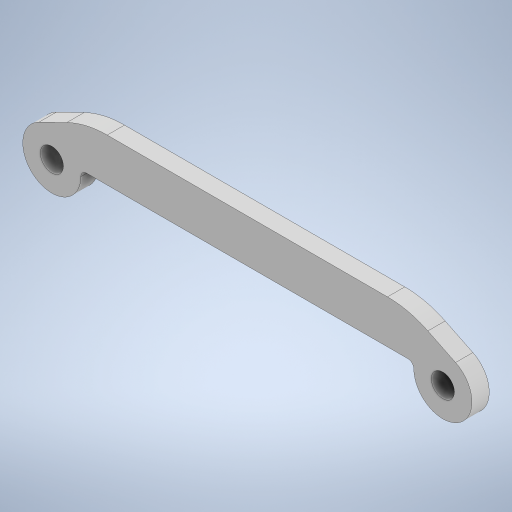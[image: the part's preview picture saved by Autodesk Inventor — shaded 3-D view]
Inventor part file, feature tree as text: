
AUTODESK INVENTOR PART (.ipt)
format: ipt  version: 2024 (Build 280153000, 153)  size: 267,776 bytes
history: native  units: in
note: dims shown in document units (in); Inventor stores cm internally (conversion verified against a paired STEP export)
features: fillet x2, extrude x1, sketch x1
ambient origin geometry x8: Origin, YZ Plane, XZ Plane, XY Plane, X Axis, Y Axis, Z Axis, Center Point
bodies: Solid1 (feature_tree)
feature tree (4):
  extrude  "Extrusion1"  Depth=0.1575in
  fillet  "Fillet1"  Radius=0.125in
  fillet  "Fillet2"  Radius=0.188in
  sketch  "Sketch1"  dims[d0=1.75in d1=0.1575in d2=0.125in d3=0.188in d4=0.25in d5=1.06in d6=0.0938in d7=0.0in d8=0.5in d9=0.032in]
